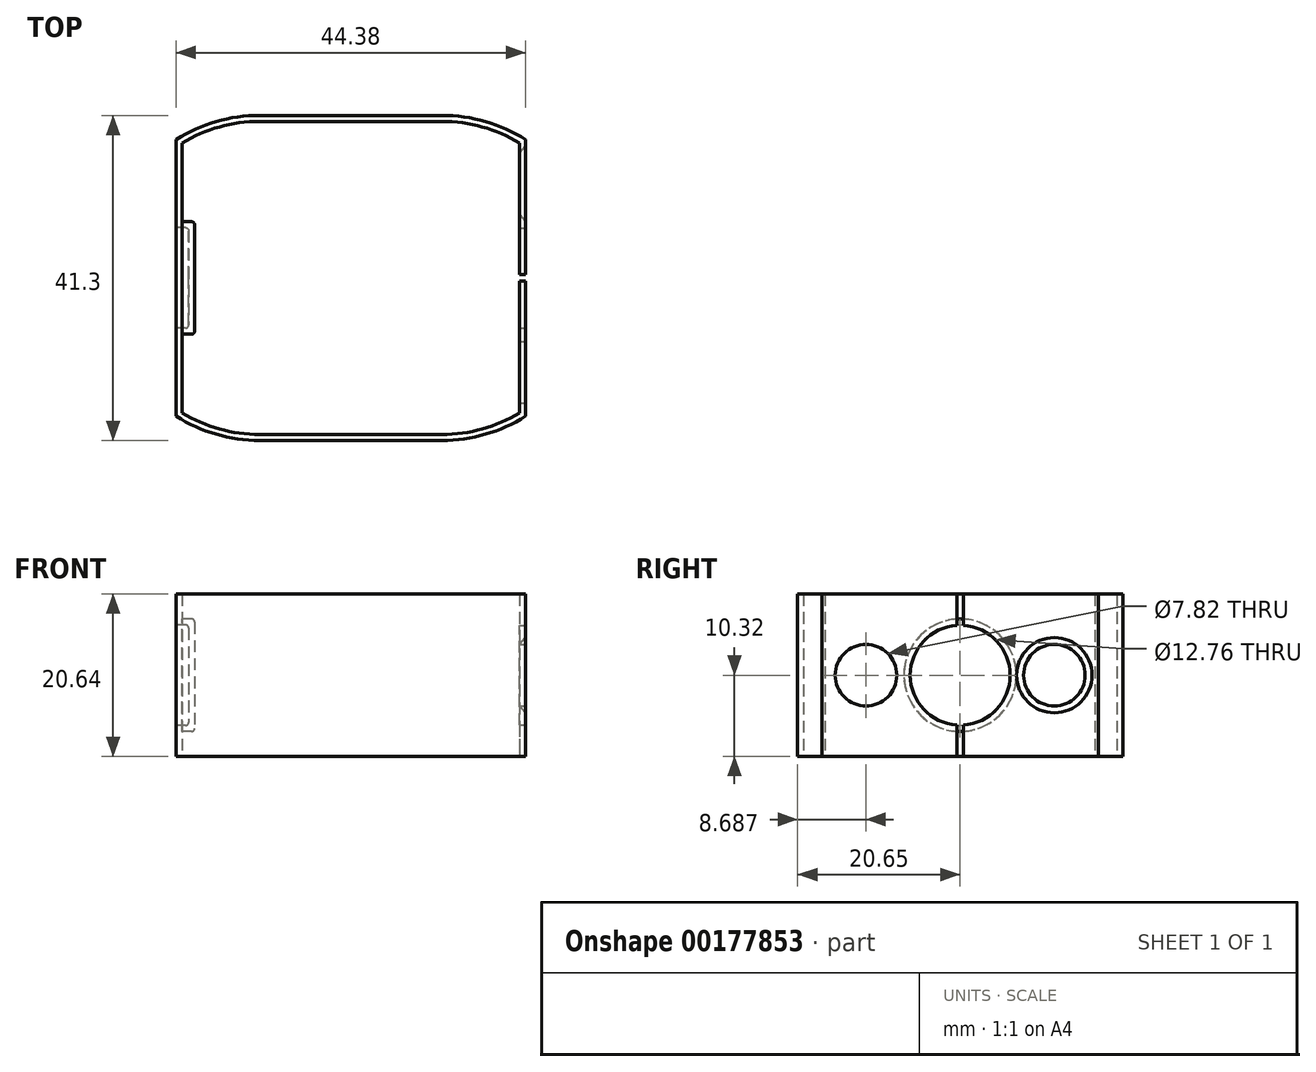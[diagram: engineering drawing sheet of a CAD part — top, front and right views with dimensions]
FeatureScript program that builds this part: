
annotation { "Feature Type Name" : "Feature", "Feature Type Description" : "" }
export const myFeature = defineFeature(function(context is Context, id is Id, definition is map)
    precondition{}
    {
        {
            var Q0;
            Q0=qCreatedBy(makeId("Top.planeOp"),FACE);
            var sketch = newSketch(context, id + "F0", { "sketchPlane" : qUnion([Q0])});
            skLineSegment(sketch, "E0.bottom", {"start": v(21.43, 17.15) * mm, "end": v(-21.43, 17.15) * mm});
            skLineSegment(sketch, "E0.top", {"start": v(21.43, -17.15) * mm, "end": v(-21.43, -17.14) * mm});
            skLineSegment(sketch, "E0.left", {"start": v(21.43, 17.14) * mm, "end": v(21.43, -17.15) * mm});
            skLineSegment(sketch, "E0.right", {"start": v(-21.43, 17.15) * mm, "end": v(-21.43, -17.15) * mm});
            skPoint(sketch, "E0.middle", {"position": v(0, 0) * mm});
            skLineSegment(sketch, "E1", {"start": v(-29.61, 0) * mm, "end": v(26.31, 0) * mm, "construction": true});
            skPoint(sketch, "E1.startSnap0", {"position": v(-21.43, 0) * mm});
            skLineSegment(sketch, "E2", {"start": v(-11.59, 19.88) * mm, "end": v(0, 19.88) * mm});
            skLineSegment(sketch, "E3", {"start": v(0, 19.88) * mm, "end": v(11.59, 19.88) * mm});
            skArc(sketch, "E4", {"start": v(-11.59, 19.88) * mm, "mid": v(-16.7, 19.19) * mm, "end": v(-21.43, 17.15) * mm});
            skArc(sketch, "E5", {"start": v(21.43, 17.14) * mm, "mid": v(16.7, 19.19) * mm, "end": v(11.59, 19.88) * mm});
            skArc(sketch, "E6.MirrorCS", {"start": v(-11.59, -19.88) * mm, "mid": v(-16.7, -19.19) * mm, "end": v(-21.43, -17.15) * mm});
            skLineSegment(sketch, "E7.MirrorCS", {"start": v(-11.59, -19.88) * mm, "end": v(0, -19.88) * mm});
            skLineSegment(sketch, "E8.MirrorCS", {"start": v(0, -19.88) * mm, "end": v(11.59, -19.88) * mm});
            skArc(sketch, "E9.MirrorCS", {"start": v(21.43, -17.15) * mm, "mid": v(16.7, -19.19) * mm, "end": v(11.59, -19.88) * mm});
            skLineSegment(sketch, "E10.0", {"start": v(-11.59, 20.65) * mm, "end": v(0, 20.65) * mm});
            skLineSegment(sketch, "E10.1", {"start": v(0, 20.65) * mm, "end": v(11.59, 20.65) * mm});
            skArc(sketch, "E10.2", {"start": v(-11.59, 20.65) * mm, "mid": v(-17.1, 19.86) * mm, "end": v(-22.2, 17.57) * mm});
            skArc(sketch, "E10.3", {"start": v(22.2, 17.57) * mm, "mid": v(17.1, 19.86) * mm, "end": v(11.59, 20.65) * mm});
            skLineSegment(sketch, "E10.4", {"start": v(22.2, 17.57) * mm, "end": v(22.2, -17.57) * mm});
            skArc(sketch, "E10.5", {"start": v(22.2, -17.57) * mm, "mid": v(17.1, -19.86) * mm, "end": v(11.59, -20.65) * mm});
            skLineSegment(sketch, "E10.6", {"start": v(-22.2, 17.57) * mm, "end": v(-22.2, -17.57) * mm});
            skArc(sketch, "E10.7", {"start": v(-11.59, -20.65) * mm, "mid": v(-17.1, -19.86) * mm, "end": v(-22.2, -17.57) * mm});
            skLineSegment(sketch, "E10.8", {"start": v(-11.59, -20.65) * mm, "end": v(0, -20.65) * mm});
            skLineSegment(sketch, "E10.9", {"start": v(0, -20.65) * mm, "end": v(11.59, -20.65) * mm});
            skSolve(sketch);
        }
        {
            var Q0;
            Q0=makeQuery(id+"F0.imprint","IMPRINT",FACE,{"disambiguationData":[TD([[makeQuery(id+"F0.imprint","IMPRINT",EDGE,{"derivedFrom":sQuery(id+"F0.wireOp",EDGE,"E0.left")}),1.0]])]});
            extrude(context, id + "F1", {"entities" : qUnion([Q0]), "endBound" : BoundingType.SYMMETRIC, "depth" : 20.64 * mm});
        }
        {
            var Q0;
            Q0=makeQuery(id+"F1.opExtrude","SWEPT_FACE",FACE,{"disambiguationData":[OSD([sQuery(id+"F0.wireOp",EDGE,"E10.4")])]});
            var sketch = newSketch(context, id + "F2", { "sketchPlane" : qUnion([Q0])});
            skCircle(sketch, "E11", {"center": v(0, 0) * mm, "radius": 6.35 * mm});
            skLineSegment(sketch, "E12.bottom", {"start": v(0.4, 16.24) * mm, "end": v(-0.4, 16.24) * mm});
            skLineSegment(sketch, "E12.top", {"start": v(0.4, -16.24) * mm, "end": v(-0.4, -16.24) * mm});
            skLineSegment(sketch, "E12.left", {"start": v(0.4, 16.24) * mm, "end": v(0.4, -16.24) * mm});
            skLineSegment(sketch, "E12.right", {"start": v(-0.4, 16.24) * mm, "end": v(-0.4, -16.24) * mm});
            skCircle(sketch, "E13", {"center": v(-11.96, 0) * mm, "radius": 3.9 * mm});
            skLineSegment(sketch, "E14", {"start": v(0, 20.34) * mm, "end": v(0, -24.58) * mm, "construction": true});
            skPoint(sketch, "E14.startSnap0", {"position": v(0, 10.32) * mm});
            skCircle(sketch, "E15.MirrorC", {"center": v(11.96, 0) * mm, "radius": 3.9 * mm});
            skSolve(sketch);
        }
        {
            var Q0;
            Q0 = qSketchRegion(id + "F2", true);
            extrude(context, id + "F3", {"entities" : qUnion([Q0]), "operationType" : NewBodyOperationType.REMOVE, "oppositeDirection" : true, "depth" : 25.4 * mm});
        }
        {
            var Q0;
            Q0 = qSketchRegion(id + "F2", true);
            extrude(context, id + "F4", {"entities" : qUnion([Q0]), "operationType" : NewBodyOperationType.REMOVE, "oppositeDirection" : true, "depth" : 25.4 * mm});
        }
        {
            var Q0;
            Q0=makeQuery(id+"F3.boolean.opBoolean","COPY",EDGE,{"derivedFrom":makeQuery(id+"F3.opExtrude","CAP_EDGE",EDGE,{"disambiguationData":[OSD([sQuery(id+"F2.wireOp",EDGE,"E13")])],"isStart":true})});
            var Q1;
            Q1=makeQuery(id+"F3.boolean.opBoolean","COPY",EDGE,{"derivedFrom":makeQuery(id+"F3.opExtrude","CAP_EDGE",EDGE,{"disambiguationData":[OSD([sQuery(id+"F2.wireOp",EDGE,"E15.MirrorC")])],"isStart":true})});
            chamfer(context, id + "F5", {"entities" : qUnion([Q0, Q1]), "chamferType" : ChamferType.OFFSET_ANGLE, "width" : 0.76 * mm, "oppositeDirection" : false, "angle" : 49 * degree, "tangentPropagation" : true});
        }
        {
            var Q0;
            Q0=makeQuery(id+"F1.opExtrude","SWEPT_FACE",FACE,{"disambiguationData":[OSD([sQuery(id+"F0.wireOp",EDGE,"E10.6")])]});
            var sketch = newSketch(context, id + "F6", { "sketchPlane" : qUnion([Q0])});
            skCircle(sketch, "E16", {"center": v(0, 0) * mm, "radius": 7.14 * mm});
            skSolve(sketch);
        }
        {
            var Q0;
            Q0 = qSketchRegion(id + "F6", true);
            extrude(context, id + "F7", {"entities" : qUnion([Q0]), "operationType" : NewBodyOperationType.ADD, "oppositeDirection" : true, "depth" : 2.35 * mm});
        }
        {
            var Q0;
            Q0=makeQuery(id+"F1.opExtrude","SWEPT_FACE",FACE,{"disambiguationData":[OSD([sQuery(id+"F0.wireOp",EDGE,"E10.6")])]});
            var sketch = newSketch(context, id + "F8", { "sketchPlane" : qUnion([Q0])});
            skCircle(sketch, "E17", {"center": v(0, 0) * mm, "radius": 6.38 * mm});
            skSolve(sketch);
        }
        {
            var Q0;
            Q0 = qSketchRegion(id + "F8", true);
            extrude(context, id + "F9", {"entities" : qUnion([Q0]), "operationType" : NewBodyOperationType.REMOVE, "oppositeDirection" : true, "depth" : 1.59 * mm});
        }
        {
            var Q0;
            Q0=makeQuery(id+"F9.boolean.opBoolean","COPY",EDGE,{"derivedFrom":makeQuery(id+"F9.opExtrude","CAP_EDGE",EDGE,{"disambiguationData":[OSD([sQuery(id+"F8.wireOp",EDGE,"E17")])],"isStart":true})});
            var Q1;
            Q1=makeQuery(id+"F9.boolean.opBoolean","COPY",EDGE,{"derivedFrom":makeQuery(id+"F9.opExtrude","CAP_EDGE",EDGE,{"disambiguationData":[OSD([sQuery(id+"F8.wireOp",EDGE,"E17")])],"isStart":false})});
            var Q2;
            Q2=makeQuery(id+"F7.opExtrude","CAP_EDGE",EDGE,{"disambiguationData":[OSD([sQuery(id+"F6.wireOp",EDGE,"E16")])],"isStart":false});
            fillet(context, id + "F10", {"entities" : qUnion([Q0, Q1, Q2]), "radius" : 0.4 * mm, "tangentPropagation" : true, "allowEdgeOverflow" : false});
        }
    });
